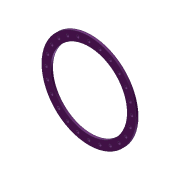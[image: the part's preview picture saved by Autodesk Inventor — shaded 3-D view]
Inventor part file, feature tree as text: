
AUTODESK INVENTOR PART (.ipt)
format: ipt  version: 2012 (Build 160160000, 160)  size: 115,712 bytes
history: native  units: in
note: dims shown in document units (in); Inventor stores cm internally (conversion verified against a paired STEP export)
features: extrude x2, sketch x2, pattern_circular x1
ambient origin geometry x8: Origin, YZ Plane, XZ Plane, XY Plane, X Axis, Y Axis, Z Axis, Center Point
bodies: Solid1 (feature_tree)
feature tree (5):
  extrude  "Extrusion1"  Depth=0.75in
  extrude  "Extrusion2"  Depth=0.375in
  pattern_circular  "Circular Pattern1"  [2 undecoded]
  sketch  "Sketch1"  dims[d0=8.0in d1=0.75in]
  sketch  "Sketch2"  dims[d2=0.1875in d3=0.0in d4=0.375in d5=0.25in d6=0.1875in d7=0.0in d8=9.4488in d9=360.0deg]
note: 2 required parameter values undecoded (feature->parameter linkage not recoverable at this tier; creation-order binding heuristic only, values carry confidence <= 0.55)
